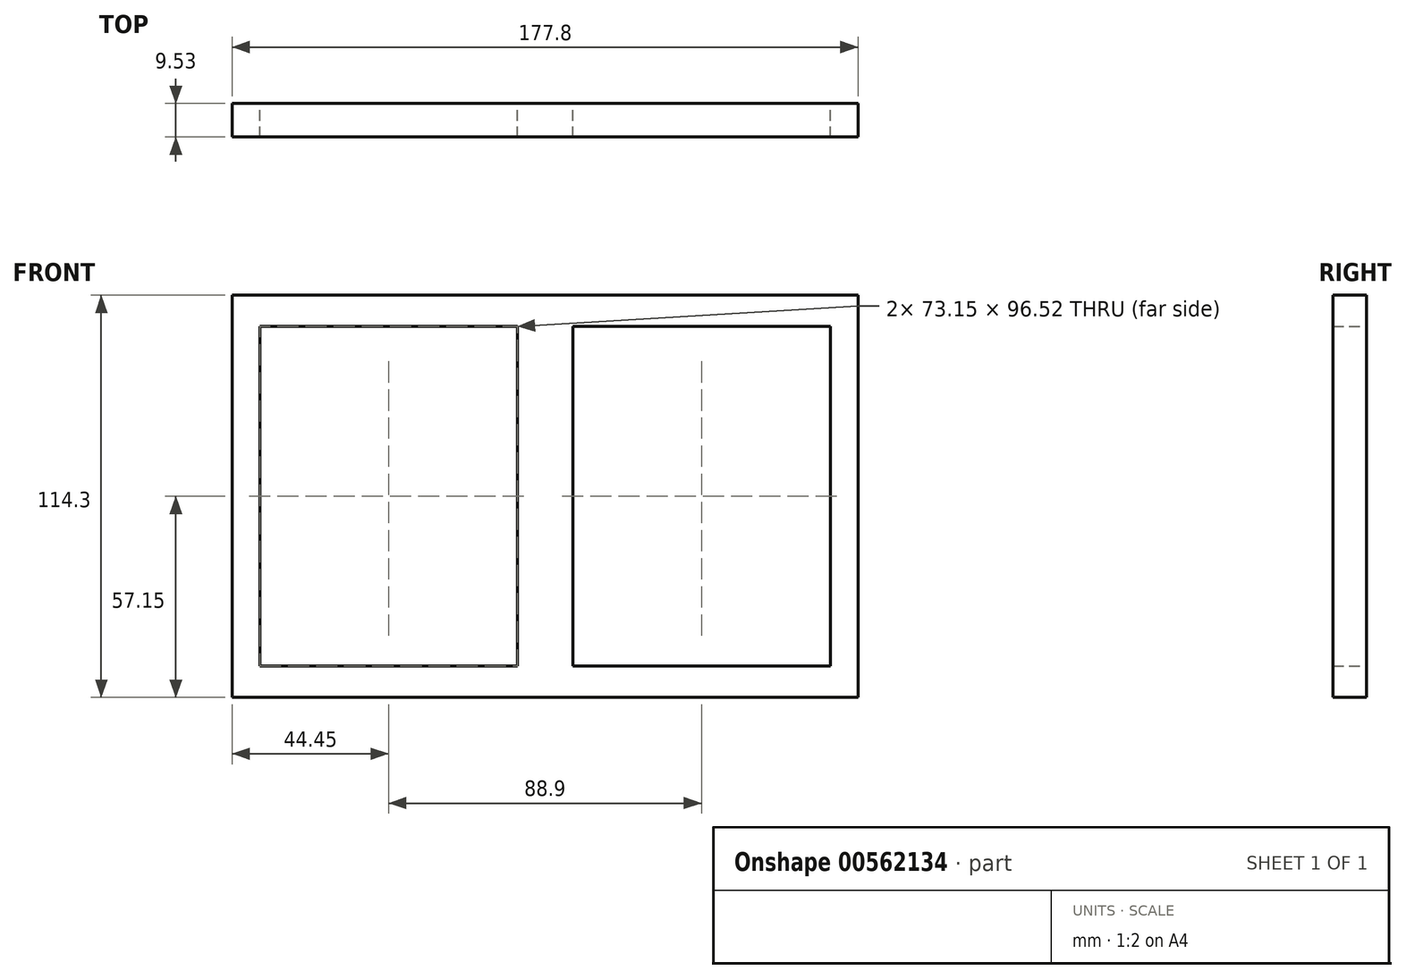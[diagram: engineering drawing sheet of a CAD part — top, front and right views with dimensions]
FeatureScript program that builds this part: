
annotation { "Feature Type Name" : "Feature", "Feature Type Description" : "" }
export const myFeature = defineFeature(function(context is Context, id is Id, definition is map)
    precondition{}
    {
        {
            var Q0;
            Q0=qCreatedBy(makeId("Front.planeOp"),FACE);
            var sketch = newSketch(context, id + "F0", { "sketchPlane" : qUnion([Q0])});
            skLineSegment(sketch, "E0.bottom", {"start": v(88.9, 57.15) * mm, "end": v(-88.9, 57.15) * mm});
            skLineSegment(sketch, "E0.top", {"start": v(88.9, -57.15) * mm, "end": v(-88.9, -57.15) * mm});
            skLineSegment(sketch, "E0.left", {"start": v(88.9, 57.15) * mm, "end": v(88.9, -57.15) * mm});
            skLineSegment(sketch, "E0.right", {"start": v(-88.9, 57.15) * mm, "end": v(-88.9, -57.15) * mm});
            skPoint(sketch, "E0.middle", {"position": v(0, 0) * mm});
            skLineSegment(sketch, "E1", {"start": v(0, 57.15) * mm, "end": v(0, -57.15) * mm, "construction": true});
            skLineSegment(sketch, "E2", {"start": v(0, 0) * mm, "end": v(88.9, 0) * mm, "construction": true});
            skPoint(sketch, "E2.endSnap0", {"position": v(88.9, 0) * mm});
            skLineSegment(sketch, "E3.bottom", {"start": v(81.03, 48.26) * mm, "end": v(7.87, 48.26) * mm});
            skLineSegment(sketch, "E3.top", {"start": v(81.03, -48.26) * mm, "end": v(7.87, -48.26) * mm});
            skLineSegment(sketch, "E3.left", {"start": v(81.03, 48.26) * mm, "end": v(81.03, -48.26) * mm});
            skLineSegment(sketch, "E3.right", {"start": v(7.87, 48.26) * mm, "end": v(7.87, -48.26) * mm});
            skPoint(sketch, "E3.middle", {"position": v(44.45, 0) * mm});
            skLineSegment(sketch, "E4.MirrorCS", {"start": v(-7.87, 48.26) * mm, "end": v(-7.87, -48.26) * mm});
            skLineSegment(sketch, "E5.MirrorCS", {"start": v(-81.03, 48.26) * mm, "end": v(-7.87, 48.26) * mm});
            skLineSegment(sketch, "E6.MirrorCS", {"start": v(-81.03, 48.26) * mm, "end": v(-81.03, -48.26) * mm});
            skLineSegment(sketch, "E7.MirrorCS", {"start": v(-81.03, -48.26) * mm, "end": v(-7.87, -48.26) * mm});
            skSolve(sketch);
        }
        {
            var Q0;
            Q0=makeQuery(id+"F0.imprint","IMPRINT",FACE,{"disambiguationData":[TD([[makeQuery(id+"F0.imprint","IMPRINT",EDGE,{"derivedFrom":sQuery(id+"F0.wireOp",EDGE,"E0.bottom")}),1.0]])]});
            extrude(context, id + "F1", {"entities" : qUnion([Q0]), "depth" : 9.52 * mm, "offsetDistance" : 25.4 * mm});
        }
    });
